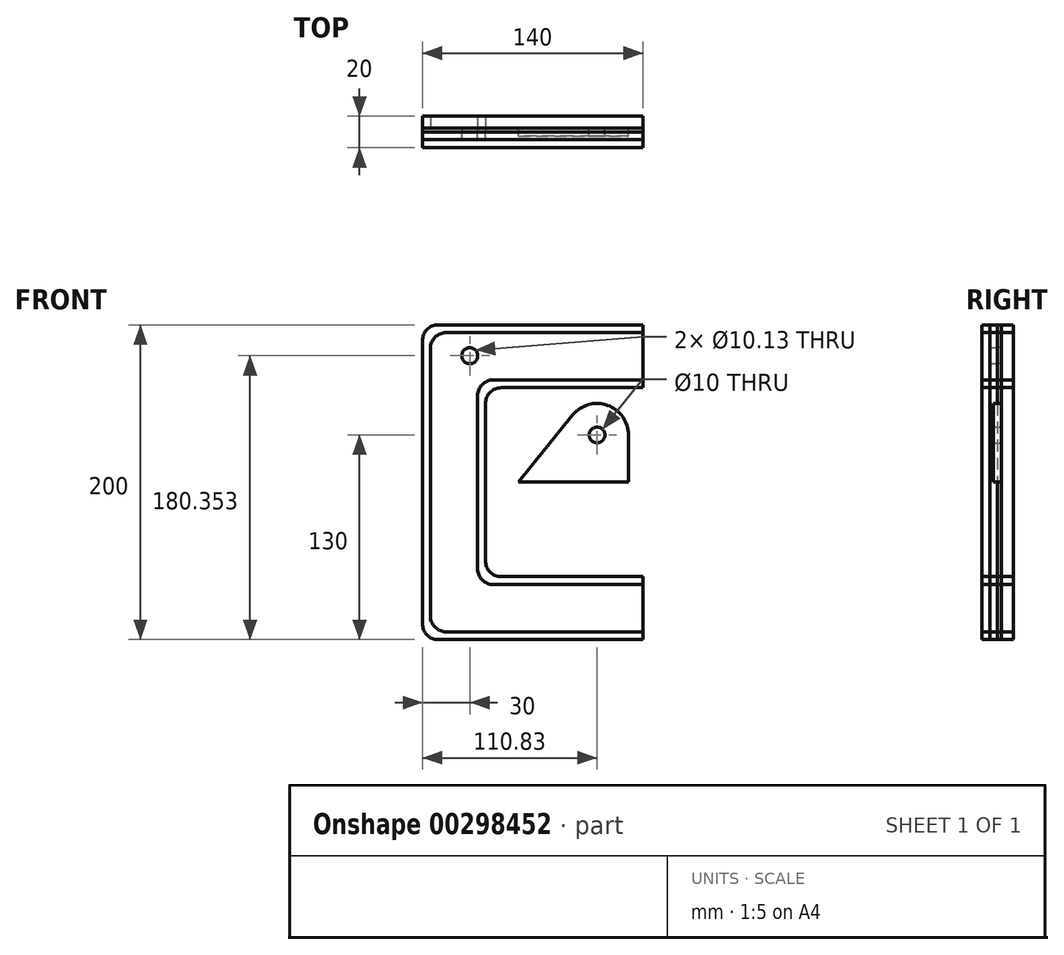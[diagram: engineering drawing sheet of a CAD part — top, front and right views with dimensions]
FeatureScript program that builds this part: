
annotation { "Feature Type Name" : "Feature", "Feature Type Description" : "" }
export const myFeature = defineFeature(function(context is Context, id is Id, definition is map)
    precondition{}
    {
        {
            var Q0;
            Q0=qCreatedBy(makeId("Front.planeOp"),FACE);
            var sketch = newSketch(context, id + "F0", { "sketchPlane" : qUnion([Q0])});
            skLineSegment(sketch, "E0", {"start": v(0, 0) * mm, "end": v(0, 50) * mm});
            skLineSegment(sketch, "E1", {"start": v(10, 60) * mm, "end": v(100, 60) * mm});
            skPoint(sketch, "E2.visualSharp", {"position": v(0, 60) * mm});
            skArc(sketch, "E2.filletArc", {"start": v(10, 60) * mm, "mid": v(2.93, 57.07) * mm, "end": v(0, 50) * mm});
            skLineSegment(sketch, "E3", {"start": v(100, 60) * mm, "end": v(100, 100) * mm});
            skLineSegment(sketch, "E4", {"start": v(100, 100) * mm, "end": v(-30, 100) * mm});
            skLineSegment(sketch, "E5", {"start": v(-40, 90) * mm, "end": v(-40, 0) * mm});
            skPoint(sketch, "E6.visualSharp", {"position": v(-40, 100) * mm});
            skArc(sketch, "E6.filletArc", {"start": v(-30, 100) * mm, "mid": v(-37.07, 97.07) * mm, "end": v(-40, 90) * mm});
            skArc(sketch, "E7.MirrorCS", {"start": v(10, -60) * mm, "mid": v(2.93, -57.07) * mm, "end": v(0, -50) * mm});
            skLineSegment(sketch, "E8.MirrorCS", {"start": v(100, -60) * mm, "end": v(100, -100) * mm});
            skLineSegment(sketch, "E9.MirrorCS", {"start": v(100, -100) * mm, "end": v(-30, -100) * mm});
            skLineSegment(sketch, "E10.MirrorCS", {"start": v(0, 0) * mm, "end": v(0, -50) * mm});
            skArc(sketch, "E11.MirrorCS", {"start": v(-30, -100) * mm, "mid": v(-37.07, -97.07) * mm, "end": v(-40, -90) * mm});
            skPoint(sketch, "E12.MirrorP", {"position": v(-40, -100) * mm});
            skPoint(sketch, "E13.MirrorP", {"position": v(0, -60) * mm});
            skLineSegment(sketch, "E14.MirrorCS", {"start": v(10, -60) * mm, "end": v(100, -60) * mm});
            skLineSegment(sketch, "E15.MirrorCS", {"start": v(-40, -90) * mm, "end": v(-40, 0) * mm});
            skCircle(sketch, "E16", {"center": v(-10, 80.35) * mm, "radius": 5.06 * mm});
            skLineSegment(sketch, "E17", {"start": v(100, 95) * mm, "end": v(-25, 95) * mm});
            skLineSegment(sketch, "E18", {"start": v(-35, 85) * mm, "end": v(-35, -85) * mm});
            skLineSegment(sketch, "E19", {"start": v(-25, -95) * mm, "end": v(100, -95) * mm});
            skPoint(sketch, "E20.visualSharp", {"position": v(-35, 95) * mm});
            skArc(sketch, "E20.filletArc", {"start": v(-25, 95) * mm, "mid": v(-32.07, 92.07) * mm, "end": v(-35, 85) * mm});
            skPoint(sketch, "E21.visualSharp", {"position": v(-35, -95) * mm});
            skArc(sketch, "E21.filletArc", {"start": v(-35, -85) * mm, "mid": v(-32.07, -92.07) * mm, "end": v(-25, -95) * mm});
            skLineSegment(sketch, "E22", {"start": v(100, 65) * mm, "end": v(5, 65) * mm});
            skLineSegment(sketch, "E23", {"start": v(-5, 55) * mm, "end": v(-5, -55) * mm});
            skLineSegment(sketch, "E24", {"start": v(5, -65) * mm, "end": v(100, -65) * mm});
            skPoint(sketch, "E25.visualSharp", {"position": v(-5, 65) * mm});
            skArc(sketch, "E25.filletArc", {"start": v(5, 65) * mm, "mid": v(-2.07, 62.07) * mm, "end": v(-5, 55) * mm});
            skPoint(sketch, "E26.visualSharp", {"position": v(-5, -65) * mm});
            skArc(sketch, "E26.filletArc", {"start": v(-5, -55) * mm, "mid": v(-2.07, -62.07) * mm, "end": v(5, -65) * mm});
            skSolve(sketch);
        }
        {
            var Q0;
            {var subQ3=sQuery(id+"F0.wireOp",EDGE,"E4");Q0=makeQuery(id+"F0.imprint","IMPRINT",FACE,{"disambiguationData":[TD([[makeQuery(id+"F0.imprint","IMPRINT",EDGE,{"derivedFrom":subQ3}),1.0]])]});}
            var Q1;
            Q1=makeQuery(id+"F0.imprint","IMPRINT",FACE,{"disambiguationData":[TD([[makeQuery(id+"F0.imprint","IMPRINT",EDGE,{"derivedFrom":sQuery(id+"F0.wireOp",EDGE,"E0")}),1.0]])]});
            extrude(context, id + "F1", {"entities" : qUnion([Q0, Q1]), "depth" : 10 * mm});
        }
        {
            var Q0;
            Q0=makeQuery(id+"F1.opExtrude","CAP_FACE",FACE,{"disambiguationData":[OSD([sQuery(id+"F0.wireOp",EDGE,"E3"),sQuery(id+"F0.wireOp",EDGE,"E4"),sQuery(id+"F0.wireOp",EDGE,"E5"),sQuery(id+"F0.wireOp",EDGE,"E6.filletArc"),sQuery(id+"F0.wireOp",EDGE,"E8.MirrorCS"),sQuery(id+"F0.wireOp",EDGE,"E9.MirrorCS"),sQuery(id+"F0.wireOp",EDGE,"E11.MirrorCS"),sQuery(id+"F0.wireOp",EDGE,"E15.MirrorCS"),sQuery(id+"F0.wireOp",EDGE,"E17"),sQuery(id+"F0.wireOp",EDGE,"E18"),sQuery(id+"F0.wireOp",EDGE,"E19"),sQuery(id+"F0.wireOp",EDGE,"E20.filletArc"),sQuery(id+"F0.wireOp",EDGE,"E21.filletArc")])],"isStart":true});
            var Q1;
            Q1=makeQuery(id+"F1.opExtrude","CAP_FACE",FACE,{"disambiguationData":[OSD([sQuery(id+"F0.wireOp",EDGE,"E0"),sQuery(id+"F0.wireOp",EDGE,"E1"),sQuery(id+"F0.wireOp",EDGE,"E2.filletArc"),sQuery(id+"F0.wireOp",EDGE,"E3"),sQuery(id+"F0.wireOp",EDGE,"E7.MirrorCS"),sQuery(id+"F0.wireOp",EDGE,"E8.MirrorCS"),sQuery(id+"F0.wireOp",EDGE,"E10.MirrorCS"),sQuery(id+"F0.wireOp",EDGE,"E14.MirrorCS"),sQuery(id+"F0.wireOp",EDGE,"E22"),sQuery(id+"F0.wireOp",EDGE,"E23"),sQuery(id+"F0.wireOp",EDGE,"E24"),sQuery(id+"F0.wireOp",EDGE,"E25.filletArc"),sQuery(id+"F0.wireOp",EDGE,"E26.filletArc")])],"isStart":true});
            extrude(context, id + "F2", {"entities" : qUnion([Q0, Q1]), "depth" : 10 * mm});
        }
        {
            var Q0;
            Q0 = qSketchRegion(id + "F0", true);
            extrude(context, id + "F3", {"entities" : qUnion([Q0]), "depth" : 5 * mm});
        }
        {
            var Q0;
            Q0=makeQuery(id+"F3.opExtrude","CAP_FACE",FACE,{"disambiguationData":[OSD([sQuery(id+"F0.wireOp",EDGE,"E0"),sQuery(id+"F0.wireOp",EDGE,"E1"),sQuery(id+"F0.wireOp",EDGE,"E2.filletArc"),sQuery(id+"F0.wireOp",EDGE,"E3"),sQuery(id+"F0.wireOp",EDGE,"E4"),sQuery(id+"F0.wireOp",EDGE,"E5"),sQuery(id+"F0.wireOp",EDGE,"E6.filletArc"),sQuery(id+"F0.wireOp",EDGE,"E7.MirrorCS"),sQuery(id+"F0.wireOp",EDGE,"E8.MirrorCS"),sQuery(id+"F0.wireOp",EDGE,"E9.MirrorCS"),sQuery(id+"F0.wireOp",EDGE,"E10.MirrorCS"),sQuery(id+"F0.wireOp",EDGE,"E11.MirrorCS"),sQuery(id+"F0.wireOp",EDGE,"E14.MirrorCS"),sQuery(id+"F0.wireOp",EDGE,"E15.MirrorCS"),sQuery(id+"F0.wireOp",EDGE,"E16")])],"isStart":true});
            extrude(context, id + "F4", {"entities" : qUnion([Q0]), "depth" : 2.5 * mm});
        }
        {
            var Q0;
            Q0=qCreatedBy(makeId("Front.planeOp"),FACE);
            var sketch = newSketch(context, id + "F5", { "sketchPlane" : qUnion([Q0])});
            skLineSegment(sketch, "E27", {"start": v(90.83, 0) * mm, "end": v(90.83, 30) * mm});
            skLineSegment(sketch, "E28", {"start": v(55.28, 42.58) * mm, "end": v(20.83, 0) * mm});
            skLineSegment(sketch, "E29", {"start": v(20.83, 0) * mm, "end": v(90.83, 0) * mm});
            skPoint(sketch, "E30.visualSharp", {"position": v(90.83, 86.51) * mm});
            skArc(sketch, "E30.filletArc", {"start": v(90.83, 30) * mm, "mid": v(77.5, 48.85) * mm, "end": v(55.28, 42.58) * mm});
            skCircle(sketch, "E31", {"center": v(70.83, 30) * mm, "radius": 5 * mm});
            skSolve(sketch);
        }
        {
            var Q0;
            Q0=makeQuery(id+"F5.imprint","IMPRINT",FACE,{"disambiguationData":[TD([[makeQuery(id+"F5.imprint","IMPRINT",EDGE,{"derivedFrom":sQuery(id+"F5.wireOp",EDGE,"E27")}),1.0]])]});
            extrude(context, id + "F6", {"entities" : qUnion([Q0]), "depth" : 2.5 * mm});
        }
        {
            var Q0;
            Q0=makeQuery(id+"F6.opExtrude","CAP_FACE",FACE,{"disambiguationData":[OSD([sQuery(id+"F5.wireOp",EDGE,"E27"),sQuery(id+"F5.wireOp",EDGE,"E28"),sQuery(id+"F5.wireOp",EDGE,"E29"),sQuery(id+"F5.wireOp",EDGE,"E30.filletArc"),sQuery(id+"F5.wireOp",EDGE,"E31")])],"isStart":true});
            extrude(context, id + "F7", {"entities" : qUnion([Q0]), "operationType" : NewBodyOperationType.ADD, "depth" : 2.5 * mm});
        }
    });
